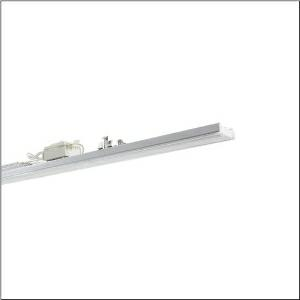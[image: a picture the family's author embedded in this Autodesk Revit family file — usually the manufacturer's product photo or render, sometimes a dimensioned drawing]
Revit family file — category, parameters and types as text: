
# Revit family: licross_r__11_recessed_mo_51te14mn49xg_de68
name_source: partatom
category: Lighting Fixtures
units: mm (PartAtom-declared; Revit-internal decimal feet)

## family parameters
Cut with Voids When Loaded = No
Host = Face
Light Source = No
Part Type = Normal
Room Calculation Point = No
Round Connector Dimension = Use Diameter
Shared = No

## types (1)
- --- (1 x LED, 9470 lm, 55.2 W, 4000K)
    Apparent Load = 55 VA
    CIE Flux Codes = 56 84 97 100 100
    Color Rendering = 80
    Color Temperature = 4000K
    Default Elevation = 1800 mm
    Description = Licross® 11 Recessed MO, luminaire insert, of sheet steel, galvanised, coil coated, white, length: 1.500mm, width: 66mm, height: 67mm, LED rated luminous flux: 9.470lm, light colour: 840, control gear: ON/OFF Multilumen, with plug, 3-pole, with phase selection, mains connection: 220..240V, AC, 50/60Hz, rated input power: 55W, internal wiring halogen-free, primary light control with lens, of plastic, primary optical cover: cover, of PMMA, light emission: direct distribution, primary light characteristic: asymmetric, protection rating (complete): IP54, insulation class (complete): insulation class I (protective earthing), certification: CE, ENEC, VDE, UKCA, protection symbol: D if used in an environment with non-conductive dust loads with corresponding accessories, impact resistance: IK06, permissible ambient temperature for indoor applications: -35..+40°C, corresponds to IFS (International Featured Standards) requirements for safety and quality in the food industry, reducing of maximum allowable ambient temperature of 5°C with ceiling mounting, packaging unit: 1 piece
    Height = 58 mm
    Lamp = 1 x LED
    Lamp Light Flux = 9470 lm
    Lamp Power = 55.2 W
    Lamp count = 1
    Length = 1500 mm
    Luminous efficacy = 172 lm/W
    Manufacturer = Siteco
    ModVariant = No
    Model = 51TE14MN49XG
    Mounting Place = Ceiling
    Mounting Type = Pendant
    Number of Poles = 1
    OnlyDefault = Yes
    Power Factor = 1
    Product Name = Licross® 11 Recessed MO
    Product group = luminaire insert | ceiling pendant
    ProductGroupID = 902
    Protection Class = Protection class I
    Protection Degree = IP 54
    RLX_Detail_Level = 1
    RLX_Emergency_Light_Flux = 0 lm
    RLX_Emergency_Type = 0
    RLX_Emergency_Type_DB = No
    RlxData = <blob elided: 22725 chars, md5=9f175e0f>
    Socket = socket
    Standby Power = 0 W
    System Light Flux = 9470 lm
    System Power = 55 W
    Type Comments = factory setting: luminous flux: 100 % | (A | C | E) | 126 mA
    Type Image = l_1296930.jpg
    URL = http://relux.com
    VarID = @adj_106757
    Voltage = 0 V
    Weight = 0.00 kg
    Width = 66 mm

## geometry (parser evidence)
native form markers: Blend x4, Sweep x11
no freeform markers — native parametric forms only
